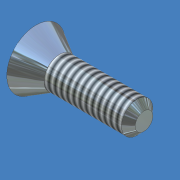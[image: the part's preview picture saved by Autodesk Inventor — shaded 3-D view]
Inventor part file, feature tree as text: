
AUTODESK INVENTOR PART (.ipt)
format: ipt  version: unknown  size: 199,680 bytes
history: native  units: mm (DEFAULTED — no unit token found)
features: sketch x2, revolve x1, chamfer x1, extrude x1, pattern_circular x1, thread x1
ambient origin geometry x8: Origin, YZ Plane, XZ Plane, XY Plane, X Axis, Y Axis, Z Axis, Center Point
feature tree (7):
  revolve  "Revolution1"  [1 undecoded]
  chamfer  "Chamfer1"  Distance=1.4605mm
  extrude  "Extrusion1"  TaperAngle=90.0deg  [1 undecoded]
  pattern_circular  "Circular Pattern1"  [2 undecoded]
  thread  "Thread1"  [1 undecoded]
  sketch  "Sketch1"  dims[d0=30.0deg d1=2.7305mm]
  sketch  "Sketch2"  dims[d2=10.0838mm d3=1.4605mm d4=90.0deg d5=0.635mm d6=3.175mm d7=0.6858mm d8=3.048mm d9=1.905mm d10=0.0mm d11=20.0mm d13=90.0deg d14=25.4mm d15=0.0mm d16=45.0deg]
note: 5 required parameter values undecoded (feature->parameter linkage not recoverable at this tier; creation-order binding heuristic only, values carry confidence <= 0.55)